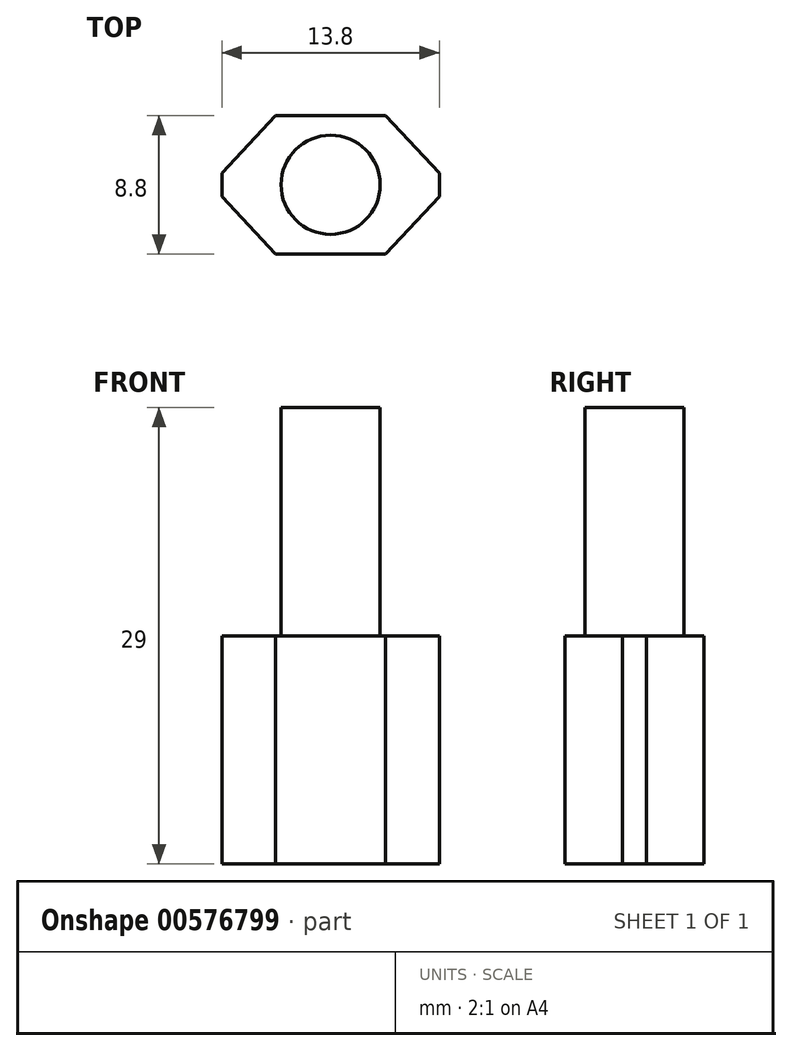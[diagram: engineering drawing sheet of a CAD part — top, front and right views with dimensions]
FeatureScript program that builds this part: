
annotation { "Feature Type Name" : "Feature", "Feature Type Description" : "" }
export const myFeature = defineFeature(function(context is Context, id is Id, definition is map)
    precondition{}
    {
        {
            var Q0;
            Q0=qCreatedBy(makeId("Top.planeOp"),FACE);
            var sketch = newSketch(context, id + "F0", { "sketchPlane" : qUnion([Q0])});
            skLineSegment(sketch, "E0", {"start": v(0, 0) * mm, "end": v(0, -4.4) * mm});
            skLineSegment(sketch, "E1", {"start": v(0, -4.4) * mm, "end": v(3.5, -4.4) * mm});
            skLineSegment(sketch, "E2", {"start": v(6.9, -0.75) * mm, "end": v(6.9, 0.75) * mm});
            skLineSegment(sketch, "E3", {"start": v(3.5, 4.4) * mm, "end": v(-3.5, 4.4) * mm});
            skLineSegment(sketch, "E4", {"start": v(-6.9, 0.75) * mm, "end": v(-6.9, -0.75) * mm});
            skLineSegment(sketch, "E5", {"start": v(-3.5, -4.4) * mm, "end": v(0, -4.4) * mm});
            skLineSegment(sketch, "E6", {"start": v(6.9, 0) * mm, "end": v(6.9, -0.75) * mm});
            skLineSegment(sketch, "E7", {"start": v(0, -4.4) * mm, "end": v(-3.5, -4.4) * mm});
            skLineSegment(sketch, "E8", {"start": v(-3.5, 4.4) * mm, "end": v(3.5, 4.4) * mm});
            skLineSegment(sketch, "E9", {"start": v(-3.5, 4.4) * mm, "end": v(-6.9, 0.75) * mm});
            skLineSegment(sketch, "E10", {"start": v(-6.9, -0.75) * mm, "end": v(-3.5, -4.4) * mm});
            skLineSegment(sketch, "E11", {"start": v(3.5, -4.4) * mm, "end": v(6.9, -0.75) * mm});
            skLineSegment(sketch, "E12", {"start": v(6.9, 0.75) * mm, "end": v(3.5, 4.4) * mm});
            skPoint(sketch, "E13.orphan", {"position": v(6.9, 4.4) * mm});
            skPoint(sketch, "E14.orphan", {"position": v(6.9, -4.4) * mm});
            skPoint(sketch, "E15.orphan", {"position": v(-6.9, -4.4) * mm});
            skSolve(sketch);
        }
        {
            var Q0;
            Q0=makeQuery(id+"F0.imprint","IMPRINT",FACE,{"disambiguationData":[TD([[makeQuery(id+"F0.imprint","IMPRINT",EDGE,{"derivedFrom":sQuery(id+"F0.wireOp",EDGE,"E4")}),1.0]])]});
            extrude(context, id + "F1", {"entities" : qUnion([Q0]), "depth" : 14.5 * mm, "offsetDistance" : 25 * mm});
        }
        {
            var Q0;
            Q0=makeQuery(id+"F1.opExtrude","CAP_FACE",FACE,{"disambiguationData":[OSD([sQuery(id+"F0.wireOp",EDGE,"E2"),sQuery(id+"F0.wireOp",EDGE,"E4"),sQuery(id+"F0.wireOp",EDGE,"E1"),sQuery(id+"F0.wireOp",EDGE,"E7"),sQuery(id+"F0.wireOp",EDGE,"E8"),sQuery(id+"F0.wireOp",EDGE,"E9"),sQuery(id+"F0.wireOp",EDGE,"E10"),sQuery(id+"F0.wireOp",EDGE,"E11"),sQuery(id+"F0.wireOp",EDGE,"E12")])],"isStart":false});
            var sketch = newSketch(context, id + "F2", { "sketchPlane" : qUnion([Q0])});
            skCircle(sketch, "E16", {"center": v(0, 0) * mm, "radius": 3.15 * mm});
            skSolve(sketch);
        }
        {
            var Q0;
            Q0 = qSketchRegion(id + "F2", true);
            extrude(context, id + "F3", {"entities" : qUnion([Q0]), "operationType" : NewBodyOperationType.ADD, "depth" : 14.5 * mm, "offsetDistance" : 25 * mm});
        }
    });
